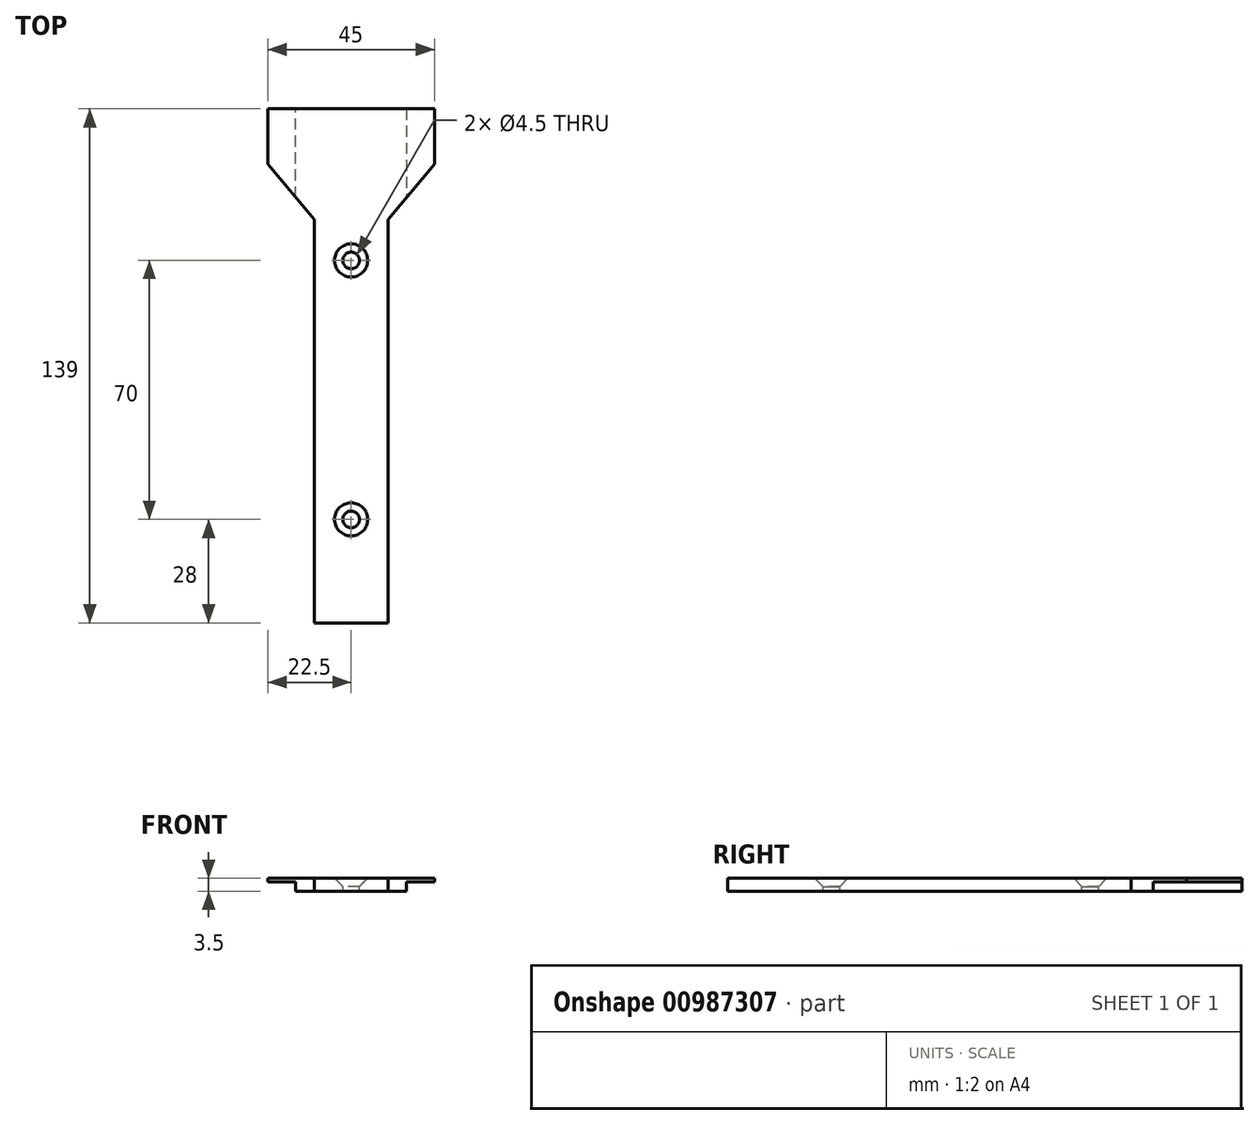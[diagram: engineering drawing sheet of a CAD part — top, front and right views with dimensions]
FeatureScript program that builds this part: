
annotation { "Feature Type Name" : "Feature", "Feature Type Description" : "" }
export const myFeature = defineFeature(function(context is Context, id is Id, definition is map)
    precondition{}
    {
        {
            var Q0;
            Q0=qCreatedBy(makeId("Top.planeOp"),FACE);
            var sketch = newSketch(context, id + "F0", { "sketchPlane" : qUnion([Q0])});
            skLineSegment(sketch, "E0.bottom", {"start": v(0, 0) * mm, "end": v(20, 0) * mm});
            skLineSegment(sketch, "E0.left", {"start": v(0, 0) * mm, "end": v(0, 109) * mm});
            skLineSegment(sketch, "E0.right", {"start": v(20, 0) * mm, "end": v(20, 109) * mm});
            skLineSegment(sketch, "E1.left", {"start": v(-12.5, 139) * mm, "end": v(-12.5, 124) * mm});
            skLineSegment(sketch, "E1.right", {"start": v(32.5, 139) * mm, "end": v(32.5, 124) * mm});
            skLineSegment(sketch, "E2", {"start": v(32.5, 124) * mm, "end": v(20, 109) * mm});
            skLineSegment(sketch, "E3", {"start": v(-12.5, 124) * mm, "end": v(0, 109) * mm});
            skLineSegment(sketch, "E4", {"start": v(-12.5, 139) * mm, "end": v(32.5, 139) * mm});
            skSolve(sketch);
        }
        {
            var Q0;
            Q0 = qSketchRegion(id + "F0", true);
            var Q1;
            Q1=makeQuery(id+"F0.imprint","IMPRINT",FACE,{"disambiguationData":[TD([[makeQuery(id+"F0.imprint","IMPRINT",EDGE,{"derivedFrom":sQuery(id+"F0.wireOp",EDGE,"E0.bottom")}),1.0]])]});
            extrude(context, id + "F1", {"entities" : qUnion([Q0, Q1]), "depth" : 3.5 * mm, "offsetDistance" : 25 * mm});
        }
        {
            var Q0;
            Q0=makeQuery(id+"F1.opExtrude","CAP_FACE",FACE,{"disambiguationData":[OSD([sQuery(id+"F0.wireOp",EDGE,"E0.bottom"),sQuery(id+"F0.wireOp",EDGE,"E0.left"),sQuery(id+"F0.wireOp",EDGE,"E0.right"),sQuery(id+"F0.wireOp",EDGE,"EQtAqdHW-yx8I-m1vf-49mE-oho1yevO6Hqp"),sQuery(id+"F0.wireOp",EDGE,"9yuLqdmx-c50i-8aJg-d5BN-at5jHRyGvICg"),sQuery(id+"F0.wireOp",EDGE,"E1.left"),sQuery(id+"F0.wireOp",EDGE,"E1.right"),sQuery(id+"F0.wireOp",EDGE,"E2"),sQuery(id+"F0.wireOp",EDGE,"E3"),sQuery(id+"F0.wireOp",EDGE,"E4")])],"isStart":true});
            var sketch = newSketch(context, id + "F2", { "sketchPlane" : qUnion([Q0])});
            skLineSegment(sketch, "E5", {"start": v(-12.5, -139) * mm, "end": v(-12.5, -124) * mm});
            skLineSegment(sketch, "E6", {"start": v(-12.5, -124) * mm, "end": v(-5, -115) * mm});
            skLineSegment(sketch, "E7", {"start": v(-5, -115) * mm, "end": v(-5, -139) * mm});
            skLineSegment(sketch, "E8", {"start": v(-5, -139) * mm, "end": v(-12.5, -139) * mm});
            skLineSegment(sketch, "E9", {"start": v(32.5, -139) * mm, "end": v(25, -139) * mm});
            skLineSegment(sketch, "E10", {"start": v(25, -139) * mm, "end": v(25, -115) * mm});
            skLineSegment(sketch, "E11", {"start": v(25, -115) * mm, "end": v(32.5, -124) * mm});
            skLineSegment(sketch, "E12", {"start": v(32.5, -124) * mm, "end": v(32.5, -139) * mm});
            skSolve(sketch);
        }
        {
            var Q0;
            Q0 = qSketchRegion(id + "F2", true);
            extrude(context, id + "F3", {"entities" : qUnion([Q0]), "operationType" : NewBodyOperationType.REMOVE, "oppositeDirection" : true, "depth" : 2.5 * mm, "offsetDistance" : 25 * mm});
        }
        {
            var Q0;
            Q0=makeQuery(id+"F1.opExtrude","CAP_FACE",FACE,{"disambiguationData":[OSD([sQuery(id+"F0.wireOp",EDGE,"E0.bottom"),sQuery(id+"F0.wireOp",EDGE,"E0.left"),sQuery(id+"F0.wireOp",EDGE,"E0.right"),sQuery(id+"F0.wireOp",EDGE,"E1.left"),sQuery(id+"F0.wireOp",EDGE,"E1.right"),sQuery(id+"F0.wireOp",EDGE,"E2"),sQuery(id+"F0.wireOp",EDGE,"E3"),sQuery(id+"F0.wireOp",EDGE,"E4")])],"isStart":false});
            var sketch = newSketch(context, id + "F4", { "sketchPlane" : qUnion([Q0])});
            skPoint(sketch, "E13", {"position": v(10, 98) * mm});
            skPoint(sketch, "E14", {"position": v(10, 28) * mm});
            skSolve(sketch);
        }
        {
            var Q0;
            Q0=sQuery(id+"F4.wireOp",VERTEX,"E13");
            var Q1;
            Q1=sQuery(id+"F4.wireOp",VERTEX,"E14");
            var Q2;
            Q2=makeQuery(id+"F1.opExtrude","SWEPT_BODY",BODY,{"disambiguationData":[OSD([sQuery(id+"F0.wireOp",EDGE,"E0.bottom"),sQuery(id+"F0.wireOp",EDGE,"E0.left"),sQuery(id+"F0.wireOp",EDGE,"E0.right"),sQuery(id+"F0.wireOp",EDGE,"E1.left"),sQuery(id+"F0.wireOp",EDGE,"E1.right"),sQuery(id+"F0.wireOp",EDGE,"E2"),sQuery(id+"F0.wireOp",EDGE,"E3"),sQuery(id+"F0.wireOp",EDGE,"E4")])]});
            hole(context, id + "F5", {"style" : HoleStyle.C_SINK, "endStyle" : HoleEndStyle.THROUGH, "standardTappedOrClearance" : lookupTablePath({ "fit" : "Normal", "standard" : "ISO", "size" : "M4", "type" : "Clearance" }), "standardBlindInLast" : lookupTablePath({ "fit" : "Normal", "standard" : "ISO", "engagement" : "75%", "pitch" : "0.7 mm", "size" : "M4", "type" : "Clearance & tapped" }), "holeDiameter" : 4.5 * mm, "cSinkDiameter" : 8.96 * mm, "cSinkAngle" : 90 * degree, "majorDiameter" : 4 * mm, "isTappedThrough" : true, "tappedDepth" : 26.25 * mm, "tapClearance" : 3, "locations" : qUnion([Q0, Q1]), "scope" : qUnion([Q2])});
        }
    });
